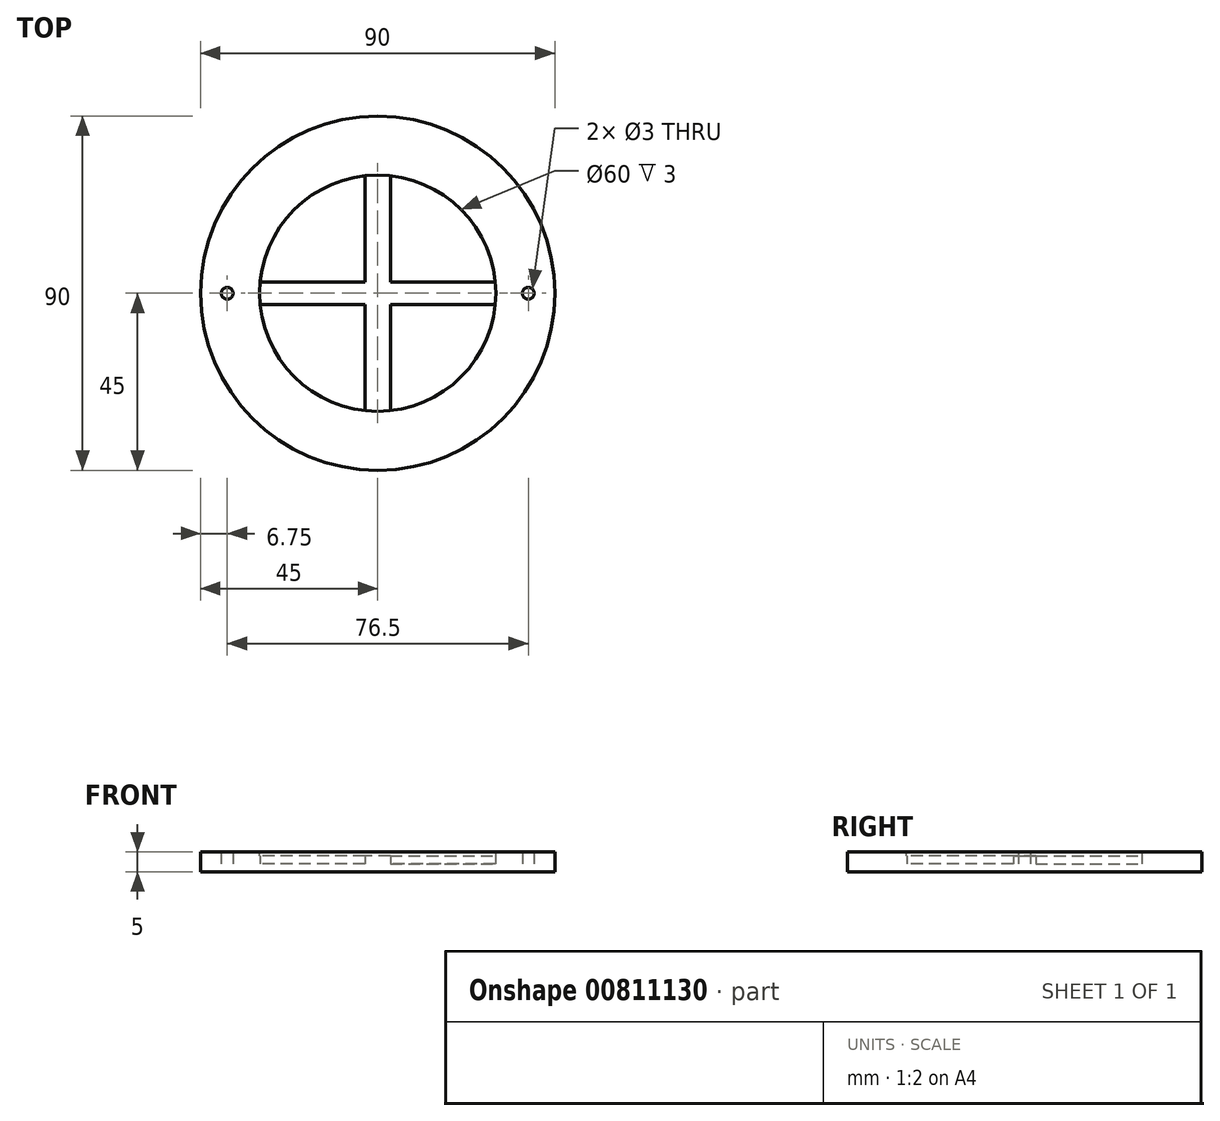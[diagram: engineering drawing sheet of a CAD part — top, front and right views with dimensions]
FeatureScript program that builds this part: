
annotation { "Feature Type Name" : "Feature", "Feature Type Description" : "" }
export const myFeature = defineFeature(function(context is Context, id is Id, definition is map)
    precondition{}
    {
        {
            var Q0;
            Q0=qCreatedBy(makeId("Top.planeOp"),FACE);
            var sketch = newSketch(context, id + "F0", { "sketchPlane" : qUnion([Q0])});
            skCircle(sketch, "E0", {"center": v(0, 0) * mm, "radius": 45 * mm});
            skCircle(sketch, "E1", {"center": v(-38.25, 0) * mm, "radius": 1.5 * mm});
            skCircle(sketch, "E2.MirrorC", {"center": v(38.25, 0) * mm, "radius": 1.5 * mm});
            skSolve(sketch);
        }
        {
            var Q0;
            Q0=makeQuery(id+"F0.imprint","IMPRINT",FACE,{"disambiguationData":[TD([[makeQuery(id+"F0.imprint","IMPRINT",EDGE,{"derivedFrom":sQuery(id+"F0.wireOp",EDGE,"E0")}),1.0]])]});
            extrude(context, id + "F1", {"entities" : qUnion([Q0]), "depth" : 5 * mm, "offsetDistance" : 25 * mm});
        }
        {
            var Q0;
            Q0=makeQuery(id+"F1.opExtrude","CAP_FACE",FACE,{"disambiguationData":[OSD([sQuery(id+"F0.wireOp",EDGE,"E0"),sQuery(id+"F0.wireOp",EDGE,"It3BDnGZ-S0hD-Hg7y-0mPw-6Rak1nUgShLr"),sQuery(id+"F0.wireOp",EDGE,"ttYtSY0M-2e0f-gOzR-NqRg-rywAT74qAXiI")])],"isStart":false});
            var sketch = newSketch(context, id + "F2", { "sketchPlane" : qUnion([Q0])});
            skCircle(sketch, "E3", {"center": v(0, 0) * mm, "radius": 30 * mm});
            skSolve(sketch);
        }
        {
            var Q0;
            Q0=makeQuery(id+"F2.imprint","IMPRINT",FACE,{"disambiguationData":[TD([[makeQuery(id+"F2.imprint","IMPRINT",EDGE,{"derivedFrom":sQuery(id+"F2.wireOp",EDGE,"E3")}),1.0]])]});
            extrude(context, id + "F3", {"entities" : qUnion([Q0]), "operationType" : NewBodyOperationType.REMOVE, "oppositeDirection" : true, "depth" : 3 * mm, "offsetDistance" : 25 * mm});
        }
        {
            var Q0;
            Q0=makeQuery(id+"F3.boolean.opBoolean","COPY",FACE,{"derivedFrom":makeQuery(id+"F3.opExtrude","CAP_FACE",FACE,{"disambiguationData":[OSD([sQuery(id+"F2.wireOp",EDGE,"E3")])],"isStart":false})});
            var sketch = newSketch(context, id + "F4", { "sketchPlane" : qUnion([Q0])});
            skLineSegment(sketch, "E4", {"start": v(-3.22, 2.86) * mm, "end": v(-3.22, 29.83) * mm});
            skLineSegment(sketch, "E5", {"start": v(-3.22, 2.86) * mm, "end": v(-29.86, 2.86) * mm});
            skLineSegment(sketch, "E6.MirrorCS", {"start": v(3.22, 2.86) * mm, "end": v(3.22, 29.83) * mm});
            skLineSegment(sketch, "E7.MirrorCS", {"start": v(-3.22, -2.86) * mm, "end": v(-29.86, -2.86) * mm});
            skLineSegment(sketch, "E8.MirrorCS", {"start": v(3.22, 2.86) * mm, "end": v(29.86, 2.86) * mm});
            skLineSegment(sketch, "E9.MirrorCS", {"start": v(3.22, -2.86) * mm, "end": v(29.86, -2.86) * mm});
            skLineSegment(sketch, "E10.MirrorCS", {"start": v(-3.22, -2.86) * mm, "end": v(-3.22, -29.83) * mm});
            skLineSegment(sketch, "E11.MirrorCS", {"start": v(3.22, -2.86) * mm, "end": v(3.22, -29.83) * mm});
            skCircle(sketch, "E12", {"center": v(0, 0) * mm, "radius": 30 * mm});
            skSolve(sketch);
        }
        {
            var Q0;
            {var subQ1=sQuery(id+"F4.wireOp",EDGE,"E4");Q0=makeQuery(id+"F4.imprint","IMPRINT",FACE,{"disambiguationData":[TD([[makeQuery(id+"F4.imprint","IMPRINT",EDGE,{"derivedFrom":subQ1}),-1.0]])]});}
            extrude(context, id + "F5", {"entities" : qUnion([Q0]), "operationType" : NewBodyOperationType.ADD, "depth" : 2 * mm, "offsetDistance" : 25 * mm});
        }
    });
